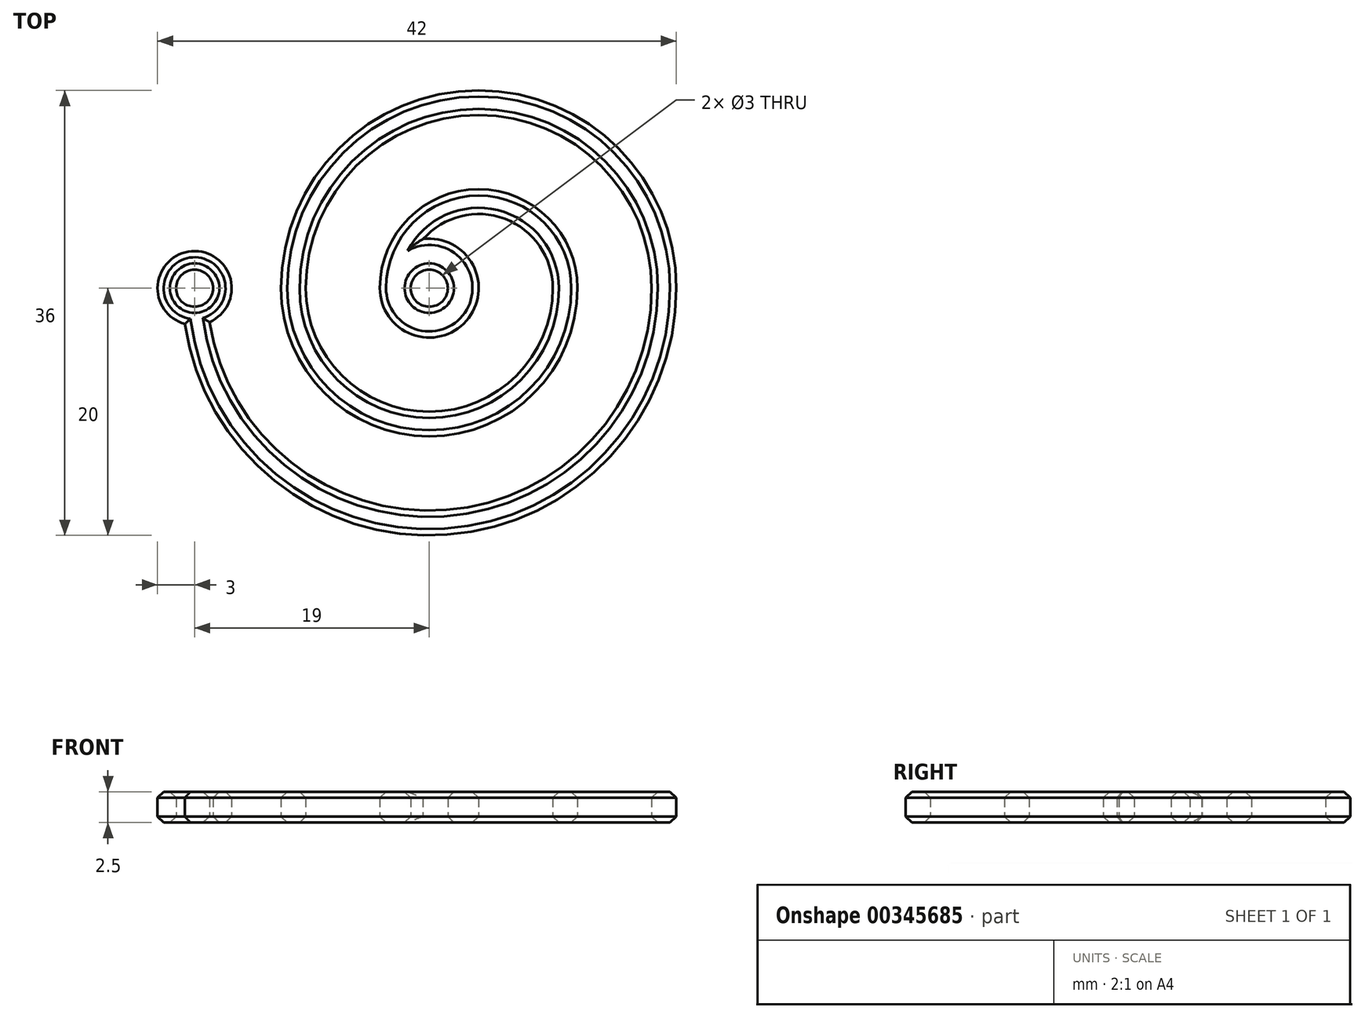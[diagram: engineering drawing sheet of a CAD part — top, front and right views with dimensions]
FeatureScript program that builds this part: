
annotation { "Feature Type Name" : "Feature", "Feature Type Description" : "" }
export const myFeature = defineFeature(function(context is Context, id is Id, definition is map)
    precondition{}
    {
        {
            var Q0;
            Q0=qCreatedBy(makeId("Top.planeOp"),FACE);
            var sketch = newSketch(context, id + "F0", { "sketchPlane" : qUnion([Q0])});
            skArc(sketch, "E0", {"start": v(12, 0) * mm, "mid": v(4, 8) * mm, "end": v(-4, 0) * mm});
            skArc(sketch, "E1", {"start": v(-12, 0) * mm, "mid": v(0, -12) * mm, "end": v(12, 0) * mm});
            skArc(sketch, "E2", {"start": v(20, 0) * mm, "mid": v(4, 16) * mm, "end": v(-12, 0) * mm});
            skArc(sketch, "E3", {"start": v(-20, 0) * mm, "mid": v(0, -20) * mm, "end": v(20, 0) * mm});
            skArc(sketch, "E4.1", {"start": v(-18, 0) * mm, "mid": v(0, -18) * mm, "end": v(18, 0) * mm});
            skArc(sketch, "E4.2", {"start": v(18, 0) * mm, "mid": v(4, 14) * mm, "end": v(-10, 0) * mm});
            skArc(sketch, "E4.3", {"start": v(-10, 0) * mm, "mid": v(0, -10) * mm, "end": v(10, 0) * mm});
            skArc(sketch, "E4.4", {"start": v(10, 0) * mm, "mid": v(6.12, 5.61) * mm, "end": v(-0.5, 3.97) * mm});
            skLineSegment(sketch, "E5", {"start": v(-20, 0) * mm, "end": v(-18, 0) * mm});
            skArc(sketch, "E6", {"start": v(-4, 0) * mm, "mid": v(3, -2.65) * mm, "end": v(-0.5, 3.97) * mm});
            skCircle(sketch, "E7", {"center": v(-19, 0) * mm, "radius": 3 * mm});
            skCircle(sketch, "E8", {"center": v(-19, 0) * mm, "radius": 1.5 * mm});
            skCircle(sketch, "E9", {"center": v(0, 0) * mm, "radius": 1.5 * mm});
            skSolve(sketch);
        }
        {
            var Q0;
            {var subQ0=sQuery(id+"F0.wireOp",EDGE,"E7");var subQ1=sQuery(id+"F0.wireOp",EDGE,"E3");var subQ2=makeQuery(id+"F0.imprint","INTERSECT",VERTEX,{"derivedFrom":[subQ1,subQ0]});Q0=makeQuery(id+"F0.imprint","IMPRINT",FACE,{"disambiguationData":[TD([[makeQuery(id+"F0.imprint","IMPRINT",EDGE,{"disambiguationData":[TD([[subQ2,1.0]])],"derivedFrom":subQ1}),-1.0]])]});}
            var Q1;
            {var subQ0=sQuery(id+"F0.wireOp",EDGE,"E7");var subQ1=sQuery(id+"F0.wireOp",EDGE,"E3");var subQ2=makeQuery(id+"F0.imprint","INTERSECT",VERTEX,{"derivedFrom":[subQ1,subQ0]});Q1=makeQuery(id+"F0.imprint","IMPRINT",FACE,{"disambiguationData":[TD([[makeQuery(id+"F0.imprint","IMPRINT",EDGE,{"disambiguationData":[TD([[subQ2,1.0]])],"derivedFrom":subQ1}),1.0]])]});}
            var Q2;
            Q2=makeQuery(id+"F0.imprint","IMPRINT",FACE,{"disambiguationData":[TD([[makeQuery(id+"F0.imprint","IMPRINT",EDGE,{"derivedFrom":sQuery(id+"F0.wireOp",EDGE,"E0")}),1.0]])]});
            extrude(context, id + "F1", {"entities" : qUnion([Q0, Q1, Q2]), "depth" : 2.5 * mm});
        }
        {
            var Q0;
            Q0=makeQuery(id+"F1.opExtrude","CAP_EDGE",EDGE,{"disambiguationData":[OSD([sQuery(id+"F0.wireOp",EDGE,"E7")])],"isStart":false});
            var Q1;
            Q1=makeQuery(id+"F1.opExtrude","CAP_EDGE",EDGE,{"disambiguationData":[OSD([sQuery(id+"F0.wireOp",EDGE,"E3")])],"isStart":false});
            var Q2;
            Q2=makeQuery(id+"F1.opExtrude","CAP_EDGE",EDGE,{"disambiguationData":[OSD([sQuery(id+"F0.wireOp",EDGE,"E4.1")])],"isStart":false});
            var Q3;
            Q3=makeQuery(id+"F1.opExtrude","CAP_EDGE",EDGE,{"disambiguationData":[OSD([sQuery(id+"F0.wireOp",EDGE,"E8")])],"isStart":false});
            var Q4;
            Q4=makeQuery(id+"F1.opExtrude","CAP_EDGE",EDGE,{"disambiguationData":[OSD([sQuery(id+"F0.wireOp",EDGE,"E9")])],"isStart":false});
            var Q5;
            Q5=makeQuery(id+"F1.opExtrude","CAP_EDGE",EDGE,{"disambiguationData":[OSD([sQuery(id+"F0.wireOp",EDGE,"E3")])],"isStart":true});
            var Q6;
            Q6=makeQuery(id+"F1.opExtrude","CAP_EDGE",EDGE,{"disambiguationData":[OSD([sQuery(id+"F0.wireOp",EDGE,"E7")])],"isStart":true});
            var Q7;
            Q7=makeQuery(id+"F1.opExtrude","CAP_EDGE",EDGE,{"disambiguationData":[OSD([sQuery(id+"F0.wireOp",EDGE,"E8")])],"isStart":true});
            var Q8;
            Q8=makeQuery(id+"F1.opExtrude","CAP_EDGE",EDGE,{"disambiguationData":[OSD([sQuery(id+"F0.wireOp",EDGE,"E9")])],"isStart":true});
            var Q9;
            Q9=makeQuery(id+"F1.opExtrude","CAP_EDGE",EDGE,{"disambiguationData":[OSD([sQuery(id+"F0.wireOp",EDGE,"E4.1")])],"isStart":true});
            chamfer(context, id + "F2", {"entities" : qUnion([Q0, Q1, Q2, Q3, Q4, Q5, Q6, Q7, Q8, Q9]), "width" : .5 * mm, "tangentPropagation" : true});
        }
    });
